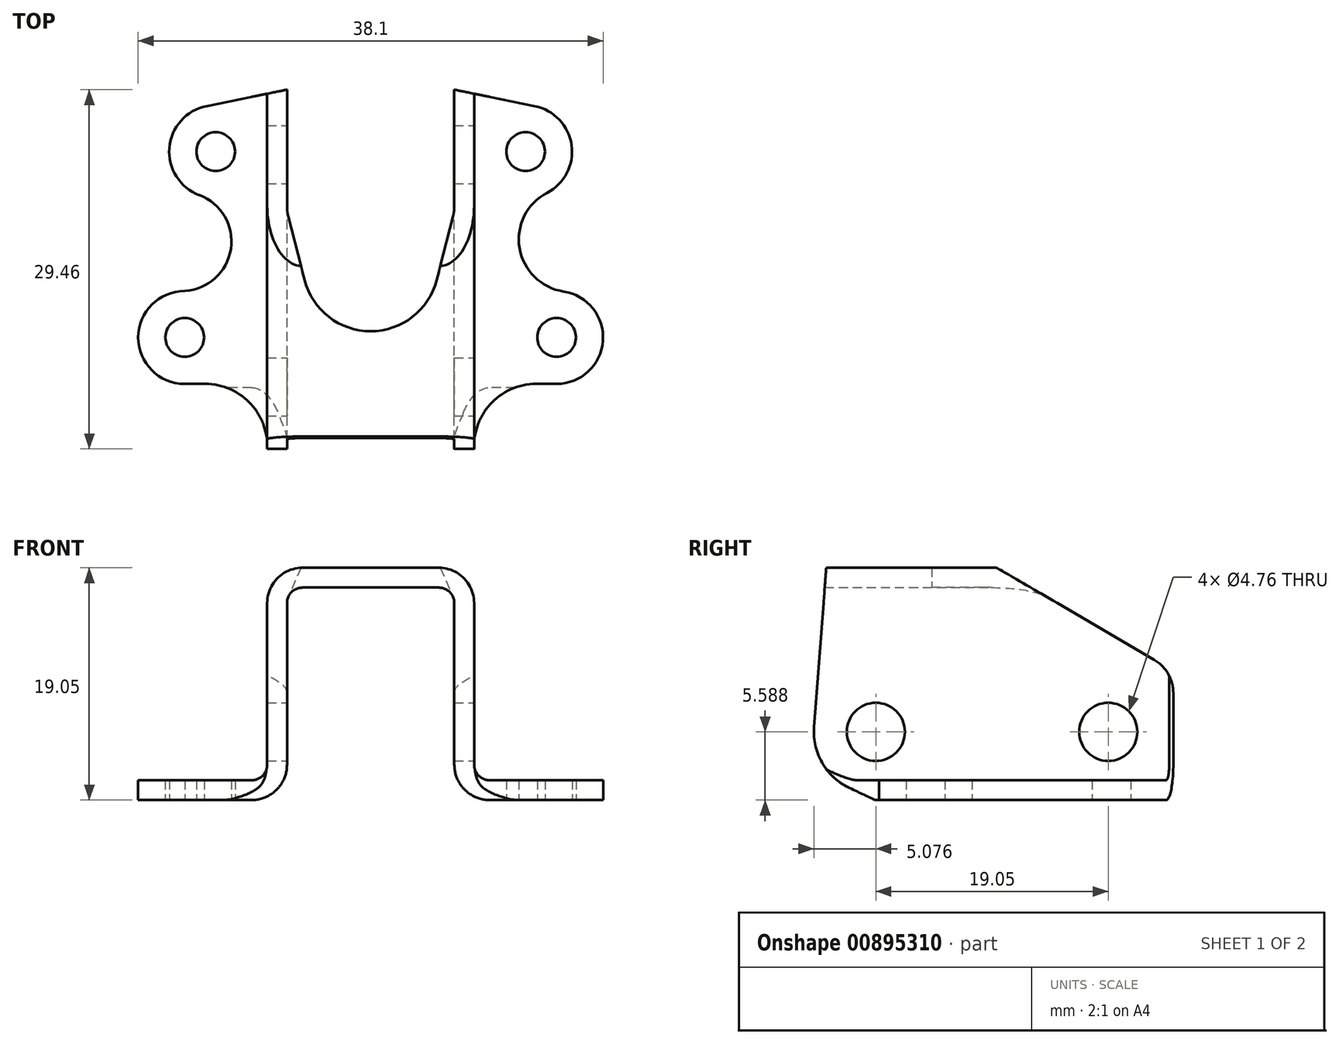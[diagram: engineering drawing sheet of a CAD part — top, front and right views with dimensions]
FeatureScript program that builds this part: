
annotation { "Feature Type Name" : "Feature", "Feature Type Description" : "" }
export const myFeature = defineFeature(function(context is Context, id is Id, definition is map)
    precondition{}
    {
        {
            var Q0;
            Q0=qCreatedBy(makeId("Front.planeOp"),FACE);
            var sketch = newSketch(context, id + "F0", { "sketchPlane" : qUnion([Q0])});
            skLineSegment(sketch, "E0", {"start": v(-33.1, 0) * mm, "end": v(-9.75, 0) * mm});
            skLineSegment(sketch, "E1", {"start": v(-6.86, 2.9) * mm, "end": v(-6.86, 16.15) * mm});
            skLineSegment(sketch, "E2", {"start": v(-5.59, 17.42) * mm, "end": v(5.59, 17.42) * mm});
            skLineSegment(sketch, "E3", {"start": v(6.86, 16.15) * mm, "end": v(6.86, 2.9) * mm});
            skLineSegment(sketch, "E4", {"start": v(9.75, 0) * mm, "end": v(35.61, 0) * mm});
            skPoint(sketch, "E5.visualSharp", {"position": v(-6.86, 0) * mm});
            skArc(sketch, "E5.filletArc", {"start": v(-9.75, 0) * mm, "mid": v(-7.7, 0.85) * mm, "end": v(-6.86, 2.9) * mm});
            skPoint(sketch, "E6.visualSharp", {"position": v(6.86, 0) * mm});
            skArc(sketch, "E6.filletArc", {"start": v(6.86, 2.9) * mm, "mid": v(7.7, 0.85) * mm, "end": v(9.75, 0) * mm});
            skPoint(sketch, "E7.visualSharp", {"position": v(6.86, 17.42) * mm});
            skArc(sketch, "E7.filletArc", {"start": v(6.86, 16.15) * mm, "mid": v(6.49, 17.05) * mm, "end": v(5.59, 17.42) * mm});
            skPoint(sketch, "E8.visualSharp", {"position": v(-6.86, 17.42) * mm});
            skArc(sketch, "E8.filletArc", {"start": v(-5.59, 17.42) * mm, "mid": v(-6.49, 17.05) * mm, "end": v(-6.86, 16.15) * mm});
            skLineSegment(sketch, "E9.0", {"start": v(9.75, 1.63) * mm, "end": v(35.61, 1.63) * mm});
            skArc(sketch, "E9.1", {"start": v(8.48, 2.9) * mm, "mid": v(8.86, 2) * mm, "end": v(9.75, 1.63) * mm});
            skLineSegment(sketch, "E9.2", {"start": v(8.48, 16.15) * mm, "end": v(8.48, 2.9) * mm});
            skArc(sketch, "E9.3", {"start": v(8.48, 16.15) * mm, "mid": v(7.64, 18.2) * mm, "end": v(5.59, 19.05) * mm});
            skLineSegment(sketch, "E9.4", {"start": v(-5.59, 19.05) * mm, "end": v(5.59, 19.05) * mm});
            skLineSegment(sketch, "E9.5", {"start": v(-33.1, 1.63) * mm, "end": v(-9.75, 1.63) * mm});
            skArc(sketch, "E9.6", {"start": v(-9.75, 1.63) * mm, "mid": v(-8.86, 2) * mm, "end": v(-8.48, 2.9) * mm});
            skLineSegment(sketch, "E9.7", {"start": v(-8.48, 2.9) * mm, "end": v(-8.48, 16.15) * mm});
            skArc(sketch, "E9.8", {"start": v(-5.59, 19.05) * mm, "mid": v(-7.64, 18.2) * mm, "end": v(-8.48, 16.15) * mm});
            skLineSegment(sketch, "E10", {"start": v(-33.1, 1.63) * mm, "end": v(-33.1, 0) * mm});
            skLineSegment(sketch, "E11", {"start": v(35.61, 1.63) * mm, "end": v(35.61, 0) * mm});
            skSolve(sketch);
        }
        {
            var Q0;
            Q0 = qSketchRegion(id + "F0", true);
            extrude(context, id + "F1", {"entities" : qUnion([Q0]), "endBound" : BoundingType.SYMMETRIC, "depth" : 50.8 * mm, "offsetDistance" : 25.4 * mm});
        }
        {
            var Q0;
            Q0=qCreatedBy(makeId("Right.planeOp"),FACE);
            var sketch = newSketch(context, id + "F2", { "sketchPlane" : qUnion([Q0])});
            skCircle(sketch, "E12", {"center": v(20.07, 5.59) * mm, "radius": 2.38 * mm});
            skCircle(sketch, "E13", {"center": v(1.02, 5.59) * mm, "radius": 2.38 * mm});
            skLineSegment(sketch, "E14", {"start": v(-32.58, 5.59) * mm, "end": v(39.65, 5.59) * mm, "construction": true});
            skLineSegment(sketch, "E15", {"start": v(31.02, 19.05) * mm, "end": v(-30.62, 19.05) * mm});
            skPoint(sketch, "E16", {"position": v(-3.05, 19.05) * mm});
            skPoint(sketch, "E17.startSnap0", {"position": v(-4.06, 6.26) * mm});
            skSolve(sketch);
        }
        {
            var Q0;
            Q0 = qSketchRegion(id + "F2", true);
            extrude(context, id + "F3", {"entities" : qUnion([Q0]), "operationType" : NewBodyOperationType.REMOVE, "endBound" : BoundingType.SYMMETRIC, "oppositeDirection" : true, "depth" : 25.4 * mm, "offsetDistance" : 25.4 * mm});
        }
        {
            var Q0;
            Q0=qCreatedBy(makeId("Right.planeOp"),FACE);
            var sketch = newSketch(context, id + "F4", { "sketchPlane" : qUnion([Q0])});
            skArc(sketch, "E18", {"start": v(-4.05, 5.98) * mm, "mid": v(-3.37, 3.03) * mm, "end": v(-1.14, 0.99) * mm});
            skLineSegment(sketch, "E19", {"start": v(-3.05, 19.05) * mm, "end": v(-4.05, 5.98) * mm});
            skLineSegment(sketch, "E20", {"start": v(10.92, 19.05) * mm, "end": v(-3.05, 19.05) * mm});
            skPoint(sketch, "E21", {"position": v(-3.05, 19.05) * mm});
            skArc(sketch, "E22", {"start": v(25.4, 8.76) * mm, "mid": v(24.98, 10.34) * mm, "end": v(23.83, 11.5) * mm});
            skPoint(sketch, "E23", {"position": v(10.92, 19.05) * mm});
            skLineSegment(sketch, "E24", {"start": v(23.83, 11.5) * mm, "end": v(10.92, 19.05) * mm});
            skLineSegment(sketch, "E25", {"start": v(0.97, 0) * mm, "end": v(-1.14, 0.99) * mm});
            skLineSegment(sketch, "E26", {"start": v(25.4, 8.76) * mm, "end": v(25.4, 0) * mm});
            skPoint(sketch, "E27.orphan", {"position": v(32.05, 0) * mm});
            skLineSegment(sketch, "E28", {"start": v(25.4, 0) * mm, "end": v(25.4, -3.72) * mm});
            skLineSegment(sketch, "E29", {"start": v(25.4, -3.72) * mm, "end": v(0.97, -3.72) * mm});
            skLineSegment(sketch, "E30", {"start": v(0.97, -3.72) * mm, "end": v(0.97, 0) * mm});
            skSolve(sketch);
        }
        {
            var Q0;
            Q0 = qSketchRegion(id + "F4", true);
            extrude(context, id + "F5", {"entities" : qUnion([Q0]), "operationType" : NewBodyOperationType.INTERSECT, "endBound" : BoundingType.SYMMETRIC, "depth" : 127 * mm, "offsetDistance" : 25.4 * mm});
        }
        {
            var Q0;
            Q0=qCreatedBy(makeId("Top.planeOp"),FACE);
            var sketch = newSketch(context, id + "F6", { "sketchPlane" : qUnion([Q0])});
            skLineSegment(sketch, "E31", {"start": v(-12.7, 36.88) * mm, "end": v(-12.7, -22.16) * mm, "construction": true});
            skLineSegment(sketch, "E32", {"start": v(12.7, 39.16) * mm, "end": v(12.7, -22.16) * mm, "construction": true});
            skLineSegment(sketch, "E33", {"start": v(-15.24, 35.4) * mm, "end": v(-15.24, -23.65) * mm, "construction": true});
            skLineSegment(sketch, "E34", {"start": v(15.24, 39.83) * mm, "end": v(15.24, -21.49) * mm, "construction": true});
            skLineSegment(sketch, "E35", {"start": v(-43.98, 20.32) * mm, "end": v(42.4, 20.32) * mm, "construction": true});
            skLineSegment(sketch, "E36", {"start": v(-44.47, 5.08) * mm, "end": v(41.91, 5.08) * mm, "construction": true});
            skCircle(sketch, "E37", {"center": v(-12.7, 20.32) * mm, "radius": 1.59 * mm});
            skCircle(sketch, "E38", {"center": v(-15.24, 5.08) * mm, "radius": 1.59 * mm});
            skCircle(sketch, "E39", {"center": v(12.7, 20.32) * mm, "radius": 1.59 * mm});
            skArc(sketch, "E40", {"start": v(-15.24, 8.9) * mm, "mid": v(-19.05, 5.08) * mm, "end": v(-15.24, 1.27) * mm});
            skCircle(sketch, "E41", {"center": v(15.24, 5.08) * mm, "radius": 1.59 * mm});
            skArc(sketch, "E42", {"start": v(15.24, 1.27) * mm, "mid": v(19.04, 4.8) * mm, "end": v(15.81, 8.85) * mm});
            skLineSegment(sketch, "E43", {"start": v(-8.48, -11.82) * mm, "end": v(-8.48, 1.27) * mm});
            skLineSegment(sketch, "E44", {"start": v(8.48, -12.98) * mm, "end": v(8.48, -8.53) * mm});
            skLineSegment(sketch, "E45", {"start": v(-15.24, 1.27) * mm, "end": v(-13.56, 1.27) * mm});
            skLineSegment(sketch, "E46", {"start": v(-8.48, 1.27) * mm, "end": v(-8.48, -8.53) * mm});
            skLineSegment(sketch, "E47", {"start": v(-8.48, -8.53) * mm, "end": v(8.48, -8.53) * mm});
            skLineSegment(sketch, "E48", {"start": v(8.48, -8.53) * mm, "end": v(8.48, 1.27) * mm});
            skLineSegment(sketch, "E49", {"start": v(13.56, 1.27) * mm, "end": v(15.24, 1.27) * mm});
            skPoint(sketch, "E50", {"position": v(-14.07, 9.14) * mm});
            skPoint(sketch, "E51", {"position": v(-11.41, 13.16) * mm});
            skArc(sketch, "E52", {"start": v(-15.24, 8.9) * mm, "mid": v(-11.46, 12.34) * mm, "end": v(-14.04, 16.75) * mm});
            skLineSegment(sketch, "E53.trimOffspring", {"start": v(8.48, 5.08) * mm, "end": v(8.48, 8.23) * mm});
            skLineSegment(sketch, "E54", {"start": v(-48.64, 11.18) * mm, "end": v(49.25, 11.18) * mm, "construction": true});
            skLineSegment(sketch, "E55", {"start": v(0, -42.72) * mm, "end": v(0, 63.97) * mm, "construction": true});
            skLineSegment(sketch, "E56", {"start": v(-17.4, 25.6) * mm, "end": v(-17.24, 25.4) * mm});
            skLineSegment(sketch, "E57", {"start": v(-8.48, -15.38) * mm, "end": v(-8.48, -3.8) * mm, "construction": true});
            skLineSegment(sketch, "E58", {"start": v(8.48, -19.13) * mm, "end": v(8.48, -3.8) * mm, "construction": true});
            skArc(sketch, "E59", {"start": v(-13.46, 24.05) * mm, "mid": v(-16.5, 20.62) * mm, "end": v(-14.04, 16.75) * mm});
            skPoint(sketch, "E60.newPointA", {"position": v(-8.48, 1.27) * mm});
            skArc(sketch, "E60.filletArc", {"start": v(-8.48, -3.8) * mm, "mid": v(-9.97, -0.22) * mm, "end": v(-13.56, 1.27) * mm});
            skArc(sketch, "E61.filletArc", {"start": v(13.56, 1.27) * mm, "mid": v(9.97, -0.22) * mm, "end": v(8.48, -3.8) * mm});
            skLineSegment(sketch, "E62", {"start": v(-6.86, 38.15) * mm, "end": v(-6.86, -12.3) * mm, "construction": true});
            skLineSegment(sketch, "E63", {"start": v(-6.86, 25.4) * mm, "end": v(-13.46, 24.05) * mm});
            skLineSegment(sketch, "E64", {"start": v(-6.86, 25.4) * mm, "end": v(-6.86, 30.16) * mm});
            skLineSegment(sketch, "E65", {"start": v(-6.86, 25.4) * mm, "end": v(-6.86, 11.1) * mm});
            skPoint(sketch, "E66", {"position": v(-1.45, 5.78) * mm});
            skLineSegment(sketch, "E67", {"start": v(-5.41, 9.79) * mm, "end": v(-6.86, 15.42) * mm});
            skArc(sketch, "E68", {"start": v(-5.59, 11.18) * mm, "mid": v(0, 5.59) * mm, "end": v(5.59, 11.18) * mm});
            skLineSegment(sketch, "E69", {"start": v(5.41, 9.79) * mm, "end": v(6.75, 15) * mm});
            skEllipticalArc(sketch, "E70.0", {});
            skEllipticalArc(sketch, "E71.0", {});
            skPoint(sketch, "E72.orphan", {"position": v(-5.59, 13.7) * mm});
            skPoint(sketch, "E73.orphan", {"position": v(5.59, 13.7) * mm});
            skPoint(sketch, "E74", {"position": v(12.14, 13.12) * mm});
            skPoint(sketch, "E75", {"position": v(14.46, 16.94) * mm});
            skArc(sketch, "E76", {"start": v(14.46, 16.94) * mm, "mid": v(12.2, 12.4) * mm, "end": v(15.81, 8.85) * mm});
            skArc(sketch, "E77", {"start": v(14.46, 16.94) * mm, "mid": v(16.47, 20.85) * mm, "end": v(13.46, 24.05) * mm});
            skLineSegment(sketch, "E78.0", {"start": v(9.75, 25.4) * mm, "end": v(35.61, 25.4) * mm});
            skLineSegment(sketch, "E79", {"start": v(6.86, 15.87) * mm, "end": v(6.86, 25.4) * mm});
            skLineSegment(sketch, "E80", {"start": v(6.86, 25.4) * mm, "end": v(13.46, 24.05) * mm});
            const initialGuessF6  = {"E70.0": [0.005588, 0.015874126721621844, 0, 1, 0.002171985404220107, 0.00127, 4.298758920199906, 4.71238898038469], "E71.0": [-0.005588, 0.015874126721621844, 0, 1, 0.002171985404220107, 0.00127, 1.5707963267948966, 1.9844263869796803]};
            skSetInitialGuess(sketch, initialGuessF6);
            skSolve(sketch);
        }
        {
            var Q0;
            Q0 = qSketchRegion(id + "F6", true);
            extrude(context, id + "F7", {"entities" : qUnion([Q0]), "operationType" : NewBodyOperationType.INTERSECT, "endBound" : BoundingType.SYMMETRIC, "depth" : 127 * mm, "offsetDistance" : 25.4 * mm});
        }
    });
